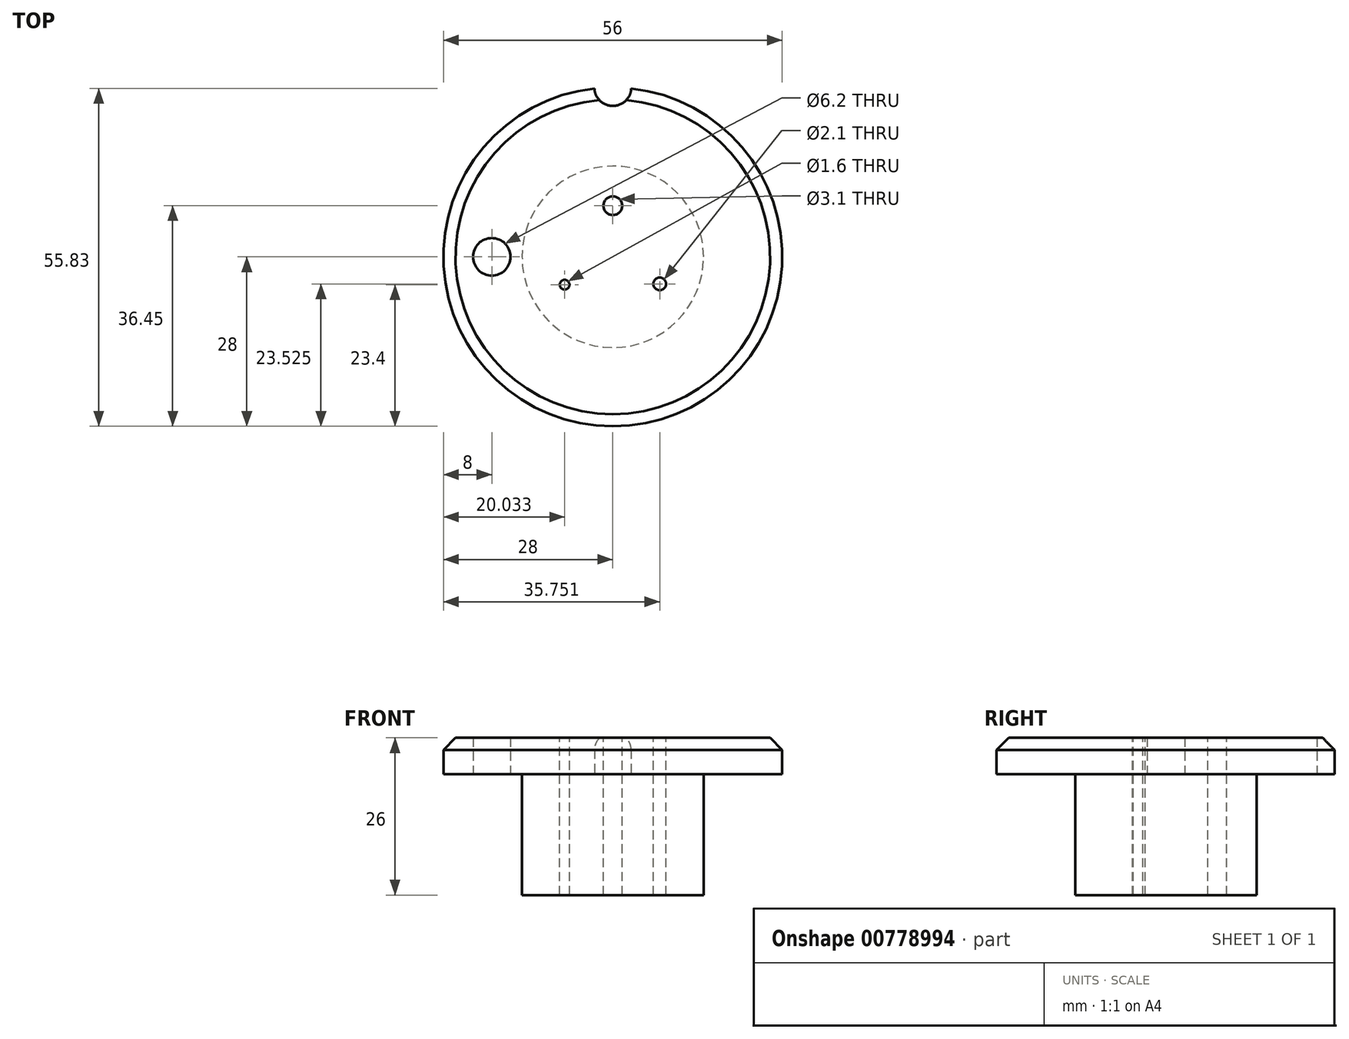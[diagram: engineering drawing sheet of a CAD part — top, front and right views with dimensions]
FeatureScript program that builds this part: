
annotation { "Feature Type Name" : "Feature", "Feature Type Description" : "" }
export const myFeature = defineFeature(function(context is Context, id is Id, definition is map)
    precondition{}
    {
        {
            var Q0;
            Q0=qCreatedBy(makeId("Front.planeOp"),FACE);
            var sketch = newSketch(context, id + "F0", { "sketchPlane" : qUnion([Q0])});
            skLineSegment(sketch, "E0", {"start": v(-15, 0) * mm, "end": v(-28, 0) * mm});
            skLineSegment(sketch, "E1", {"start": v(-28, 0) * mm, "end": v(-28, 6) * mm});
            skLineSegment(sketch, "E2", {"start": v(-28, 6) * mm, "end": v(0, 6) * mm});
            skLineSegment(sketch, "E3", {"start": v(0, 6) * mm, "end": v(0, -20) * mm});
            skLineSegment(sketch, "E4", {"start": v(0, -20) * mm, "end": v(-15, -20) * mm});
            skLineSegment(sketch, "E5", {"start": v(-15, -20) * mm, "end": v(-15, 0) * mm});
            skSolve(sketch);
        }
        {
            var Q0;
            Q0=makeQuery(id+"F0.imprint","IMPRINT",FACE,{"disambiguationData":[TD([[makeQuery(id+"F0.imprint","IMPRINT",EDGE,{"derivedFrom":sQuery(id+"F0.wireOp",EDGE,"E0")}),-1.0]])]});
            var Q1;
            Q1=sQuery(id+"F0.wireOp",EDGE,"E3");
            revolve(context, id + "F1", {"surfaceOperationType" : NewSurfaceOperationType.NEW, "entities" : qUnion([Q0]), "axis" : qUnion([Q1]), "revolveType" : RevolveType.FULL});
        }
        {
            var Q0;
            Q0=makeQuery(id+"F1.opRevolve","SWEPT_EDGE",EDGE,{"disambiguationData":[OSD([sQuery(id+"F0.wireOp",EDGE,"E1"),sQuery(id+"F0.wireOp",EDGE,"E2")])]});
            chamfer(context, id + "F2", {"entities" : qUnion([Q0]), "width" : 2 * mm, "tangentPropagation" : true});
        }
        {
            var Q0;
            Q0=qCreatedBy(makeId("Top.planeOp"),FACE);
            var sketch = newSketch(context, id + "F3", { "sketchPlane" : qUnion([Q0])});
            skCircle(sketch, "E6", {"center": v(0, 28) * mm, "radius": 3.05 * mm});
            skSolve(sketch);
        }
        {
            var Q0;
            Q0 = qSketchRegion(id + "F3", true);
            var Q1;
            Q1=makeQuery(id+"F1.opRevolve","SWEPT_FACE",FACE,{"disambiguationData":[OSD([sQuery(id+"F0.wireOp",EDGE,"E2")])]});
            extrude(context, id + "F4", {"entities" : qUnion([Q0]), "operationType" : NewBodyOperationType.REMOVE, "endBound" : BoundingType.UP_TO_SURFACE, "depth" : 25 * mm, "endBoundEntityFace" : qUnion([Q1]), "offsetDistance" : 25 * mm});
        }
        {
            var Q0;
            Q0=qCreatedBy(makeId("Top.planeOp"),FACE);
            var sketch = newSketch(context, id + "F5", { "sketchPlane" : qUnion([Q0])});
            skCircle(sketch, "E7", {"center": v(-20, 0) * mm, "radius": 3.1 * mm});
            skSolve(sketch);
        }
        {
            var Q0;
            Q0 = qSketchRegion(id + "F5", true);
            var Q1;
            Q1=makeQuery(id+"F1.opRevolve","SWEPT_FACE",FACE,{"disambiguationData":[OSD([sQuery(id+"F0.wireOp",EDGE,"E2")])]});
            extrude(context, id + "F6", {"entities" : qUnion([Q0]), "operationType" : NewBodyOperationType.REMOVE, "endBound" : BoundingType.UP_TO_SURFACE, "depth" : 25 * mm, "endBoundEntityFace" : qUnion([Q1]), "offsetDistance" : 25 * mm});
        }
        {
            var Q0;
            Q0=qCreatedBy(makeId("Top.planeOp"),FACE);
            var sketch = newSketch(context, id + "F7", { "sketchPlane" : qUnion([Q0])});
            skCircle(sketch, "E8", {"center": v(0, 0) * mm, "radius": 10 * mm, "construction": true});
            skCircle(sketch, "E9", {"center": v(0, 8.45) * mm, "radius": 1.55 * mm});
            skCircle(sketch, "E10", {"center": v(-7.97, -4.6) * mm, "radius": 0.8 * mm});
            skCircle(sketch, "E11", {"center": v(7.75, -4.47) * mm, "radius": 1.05 * mm});
            skLineSegment(sketch, "E12", {"start": v(-7.97, -4.6) * mm, "end": v(0, 0) * mm, "construction": true});
            skLineSegment(sketch, "E13", {"start": v(0, 0) * mm, "end": v(7.75, -4.48) * mm, "construction": true});
            skSolve(sketch);
        }
        {
            var Q0;
            Q0 = qSketchRegion(id + "F7", true);
            var Q1;
            Q1=makeQuery(id+"F1.opRevolve","SWEPT_FACE",FACE,{"disambiguationData":[OSD([sQuery(id+"F0.wireOp",EDGE,"E4")])]});
            var Q2;
            Q2=makeQuery(id+"F1.opRevolve","SWEPT_FACE",FACE,{"disambiguationData":[OSD([sQuery(id+"F0.wireOp",EDGE,"E2")])]});
            extrude(context, id + "F8", {"entities" : qUnion([Q0]), "operationType" : NewBodyOperationType.REMOVE, "endBound" : BoundingType.UP_TO_SURFACE, "oppositeDirection" : true, "depth" : 25 * mm, "endBoundEntityFace" : qUnion([Q1]), "offsetDistance" : 25 * mm, "hasSecondDirection" : true, "secondDirectionBound" : SecondDirectionBoundingType.UP_TO_SURFACE, "secondDirectionOppositeDirection" : false, "secondDirectionDepth" : 25 * mm, "secondDirectionBoundEntityFace" : qUnion([Q2])});
        }
    });
